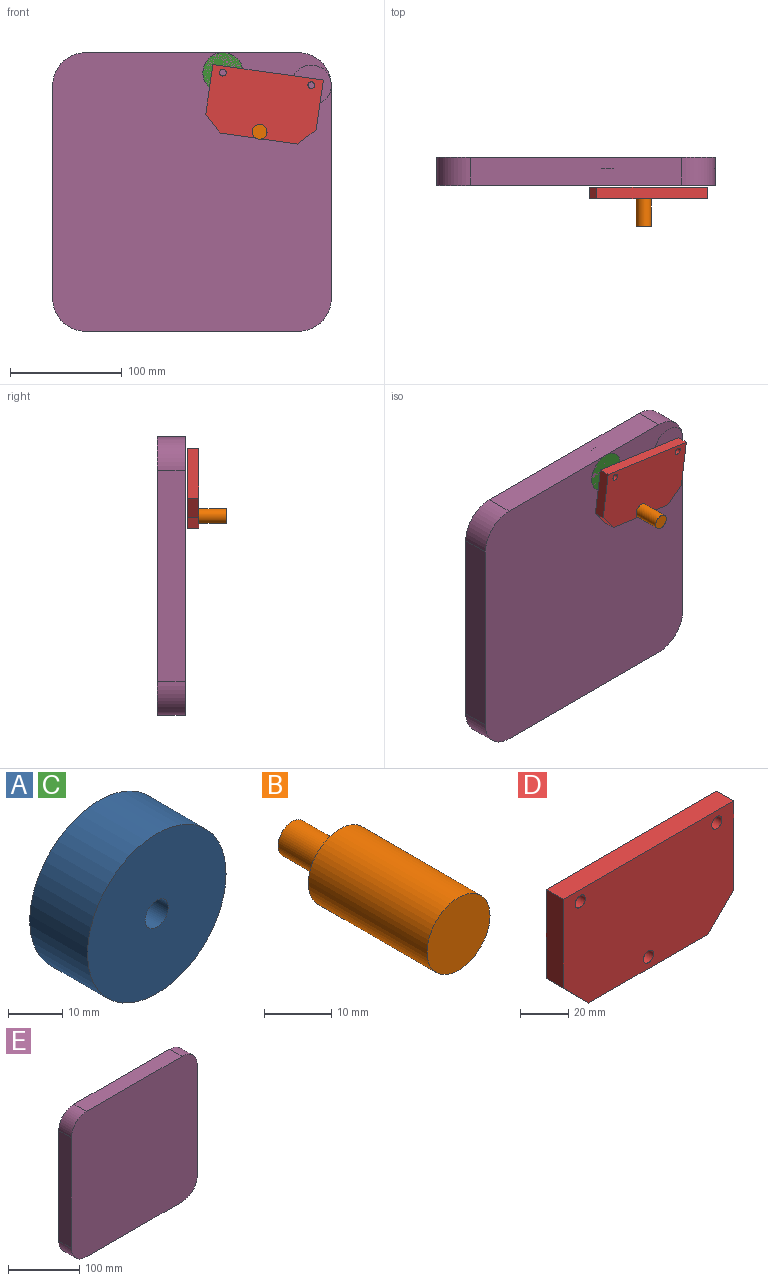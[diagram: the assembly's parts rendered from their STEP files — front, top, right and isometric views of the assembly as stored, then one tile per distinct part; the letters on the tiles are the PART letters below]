
ASSEMBLY  parts=5 mates=5
PART A: 4 faces, bbox 36x15x36 mm
  f0: cylinder r=3mm len=15mm, axis (0,1,0), area 282.7mm2, adj f2,f3
  f1: cylinder r=18mm len=36mm, axis (0,1,0), area 1696.5mm2, adj f2,f3
  f2: plane 36x36mm, normal (0,-1,0), area 989.6mm2, adj f0,f1
  f3: plane 36x36mm, normal (0,1,0), area 989.6mm2, adj f0,f1
PART B: 5 faces, bbox 13.3x35x13.3 mm
  f0: cylinder r=3mm len=10mm, axis (0,-1,0), area 188.5mm2, adj f1,f4
  f1: plane 6x6mm, normal (0,1,0), area 28.3mm2, adj f0
  f2: cylinder r=6.63mm len=25mm, axis (0,1,0), area 1041mm2, adj f3,f4
  f3: plane 13.25x13.25mm, normal (0,-1,0), area 138mm2, adj f2
  f4: plane 13.25x13.25mm, normal (0,1,0), area 109.7mm2, adj f0,f2
PART C: same geometry as A
PART D: 11 faces, bbox 100x10x60 mm
  f0: plane 45x10mm, normal (-1,0,0), area 450mm2, adj f3,f4,f5,f9
  f1: plane 70x10mm, normal (0,0,-1), area 700mm2, adj f4,f5,f9,f10
  f2: plane 45x10mm, normal (1,0,0), area 450mm2, adj f3,f4,f5,f10
  f3: plane 100x10mm, normal (0,0,1), area 1000mm2, adj f0,f2,f4,f5
  f4: plane 100x60mm, normal (0,-1,0), area 5690.2mm2, adj f0,f1,f2,f3,f6,f7,f8,f9
  f5: plane 100x60mm, normal (0,1,0), area 5690.2mm2, adj f0,f1,f2,f3,f6,f7,f8,f9
  f6: cylinder r=3mm len=10mm, axis (0,-1,0), area 188.5mm2, adj f4,f5
  f7: cylinder r=3mm len=10mm, axis (0,-1,0), area 188.5mm2, adj f4,f5
  f8: cylinder r=3mm len=10mm, axis (0,-1,0), area 188.5mm2, adj f4,f5
  f9: plane 15x15mm, normal (-0.71,0,-0.71), area 212.1mm2, adj f0,f1,f4,f5
  f10: plane 15x15mm, normal (0.71,0,-0.71), area 212.1mm2, adj f1,f2,f4,f5
PART E: 10 faces, bbox 250x25x250 mm
  f0: plane 190x25mm, normal (0,0,-1), area 4750mm2, adj f1,f7,f8,f9
  f1: cylinder r=30mm len=30mm, axis (0,-1,0), area 1178.1mm2, adj f0,f2,f8,f9
  f2: plane 190x25mm, normal (1,0,0), area 4750mm2, adj f1,f3,f8,f9
  f3: cylinder r=30mm len=30mm, axis (0,-1,0), area 1178.1mm2, adj f2,f4,f8,f9
  f4: plane 190x25mm, normal (0,0,1), area 4750mm2, adj f3,f5,f8,f9
  f5: cylinder r=30mm len=30mm, axis (0,-1,0), area 1178.1mm2, adj f4,f6,f8,f9
  f6: plane 190x25mm, normal (-1,0,0), area 4750mm2, adj f5,f7,f8,f9
  f7: cylinder r=30mm len=30mm, axis (0,-1,0), area 1178.1mm2, adj f0,f6,f8,f9
  f8: plane 250x250mm, normal (0,1,0), area 61727.4mm2, adj f0,f1,f2,f3,f4,f5,f6,f7
  f9: plane 250x250mm, normal (0,-1,0), area 61727.4mm2, adj f0,f1,f2,f3,f4,f5,f6,f7
PLACE A rot(axis=(0,-1,0),124.5deg) t=(107.28,3.1,96.41)mm
PLACE B rot(axis=(0,1,0),8.1deg) t=(46.78,-13.9,-45.51)mm
PLACE C rot(axis=(0,-1,0),8deg) t=(28.07,3.1,107.63)mm
PLACE D rot(axis=(0,1,0),8.1deg) t=(46.78,-13.9,-45.51)mm
PLACE E t=(0.31,-11.9,0.63)mm fixed
MATE fastened B.f0 <-> D.f7  axis (0,1,0) through (60.95,-23.9,54.49)mm
MATE planar C.f0 <-> E.f9  axis (0,-1,0) through (28.07,-11.9,107.63)mm
MATE revolute C.f0 <-> D.f8  axis (0,-1,0) through (28.07,-11.9,107.63)mm
MATE planar A.f0 <-> E.f9  axis (0,-1,0) through (107.28,-11.9,96.41)mm
MATE revolute D.f6 <-> A.f0  axis (0,-1,0) through (107.28,-13.9,96.41)mm
